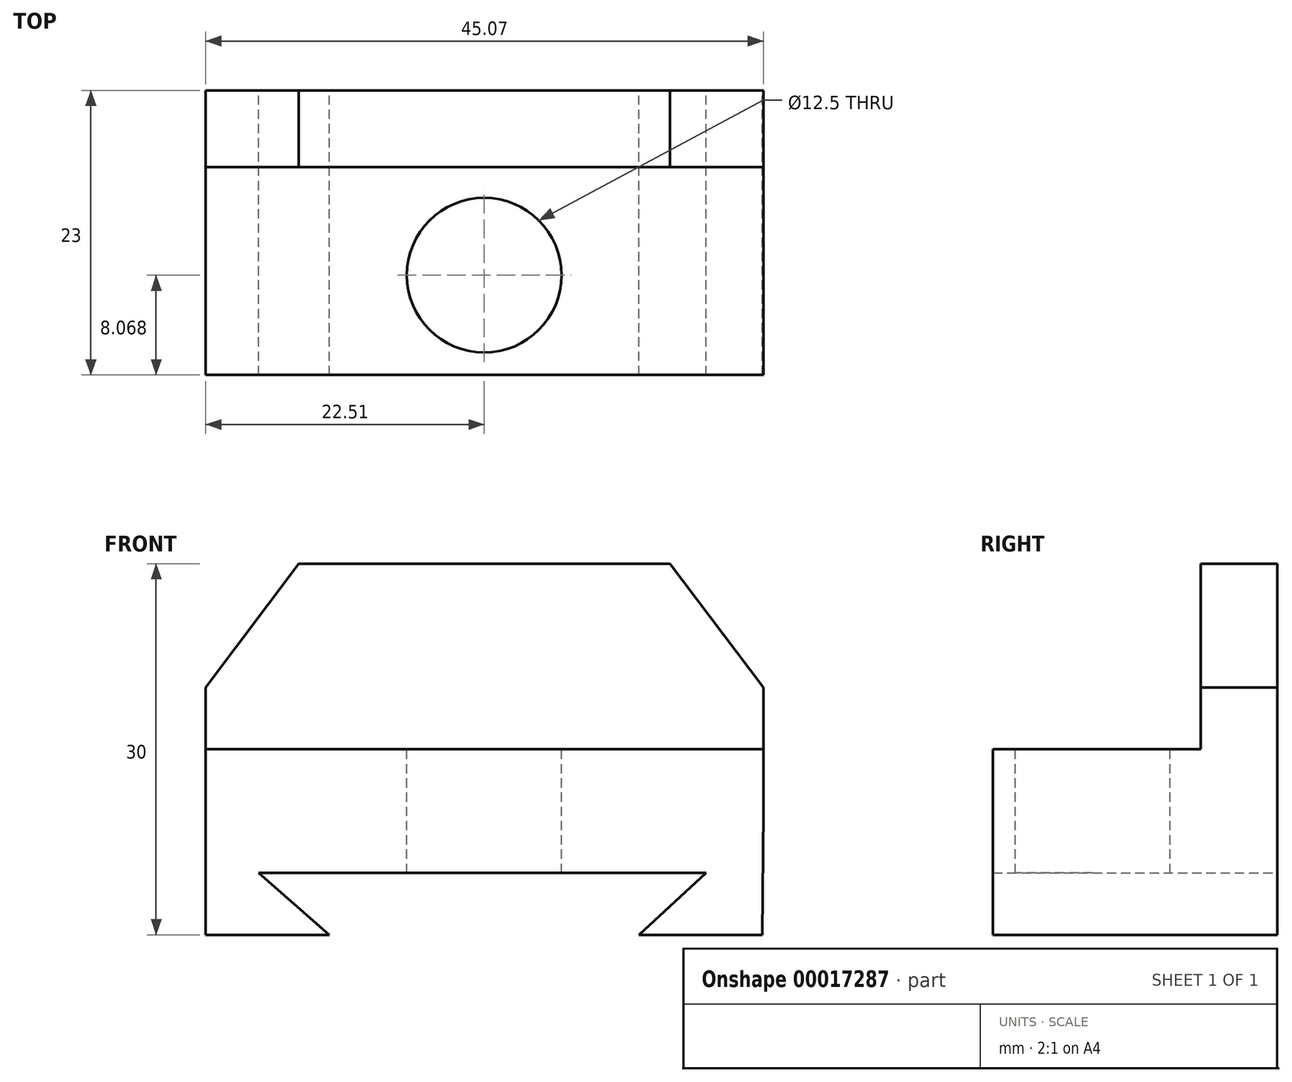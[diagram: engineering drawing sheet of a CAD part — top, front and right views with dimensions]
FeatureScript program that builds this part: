
annotation { "Feature Type Name" : "Feature", "Feature Type Description" : "" }
export const myFeature = defineFeature(function(context is Context, id is Id, definition is map)
    precondition{}
    {
        {
            var Q0;
            Q0=qCreatedBy(makeId("Front.planeOp"),FACE);
            var sketch = newSketch(context, id + "F0", { "sketchPlane" : qUnion([Q0])});
            skLineSegment(sketch, "E0", {"start": v(22.49, -30) * mm, "end": v(22.56, -20) * mm});
            skLineSegment(sketch, "E1", {"start": v(22.56, -20) * mm, "end": v(22.56, -15) * mm});
            skLineSegment(sketch, "E2", {"start": v(-22.58, -30.8) * mm, "end": v(-22.51, -30) * mm});
            skLineSegment(sketch, "E3", {"start": v(-22.51, -30) * mm, "end": v(-22.51, -20) * mm});
            skLineSegment(sketch, "E4", {"start": v(-22.51, -20) * mm, "end": v(-22.51, -15) * mm});
            skLineSegment(sketch, "E5", {"start": v(-22.51, -15) * mm, "end": v(22.56, -15) * mm});
            skLineSegment(sketch, "E6", {"start": v(-22.51, -15) * mm, "end": v(-22.51, -10) * mm});
            skLineSegment(sketch, "E7", {"start": v(22.56, -15) * mm, "end": v(22.56, -10) * mm});
            skLineSegment(sketch, "E8", {"start": v(0, 0) * mm, "end": v(15, 0) * mm});
            skLineSegment(sketch, "E9", {"start": v(0, 0) * mm, "end": v(-15, 0) * mm});
            skLineSegment(sketch, "E10", {"start": v(-22.51, -10) * mm, "end": v(-15, 0) * mm});
            skLineSegment(sketch, "E11", {"start": v(15, 0) * mm, "end": v(22.56, -10) * mm});
            skLineSegment(sketch, "E12", {"start": v(-22.51, -30) * mm, "end": v(-12.51, -30) * mm});
            skLineSegment(sketch, "E13", {"start": v(22.49, -30) * mm, "end": v(12.49, -30) * mm});
            skLineSegment(sketch, "E14", {"start": v(-12.51, -30) * mm, "end": v(-18.22, -25) * mm});
            skLineSegment(sketch, "E15", {"start": v(12.49, -30) * mm, "end": v(17.92, -25) * mm});
            skLineSegment(sketch, "E16", {"start": v(17.92, -25) * mm, "end": v(-18.22, -25) * mm});
            skSolve(sketch);
        }
        {
            var Q0;
            Q0=makeQuery(id+"F0.imprint","IMPRINT",FACE,{"disambiguationData":[TD([[makeQuery(id+"F0.imprint","IMPRINT",EDGE,{"derivedFrom":sQuery(id+"F0.wireOp",EDGE,"E0")}),1.0]])]});
            extrude(context, id + "F1", {"entities" : qUnion([Q0]), "depth" : 23 * mm});
        }
        {
            var Q0;
            Q0=makeQuery(id+"F0.imprint","IMPRINT",FACE,{"disambiguationData":[TD([[makeQuery(id+"F0.imprint","IMPRINT",EDGE,{"derivedFrom":sQuery(id+"F0.wireOp",EDGE,"E5")}),1.0]])]});
            var sketch = newSketch(context, id + "F2", { "sketchPlane" : qUnion([Q0])});
            skSolve(sketch);
        }
        {
            var Q0;
            Q0 = qSketchRegion(id + "F2", true);
            var Q1;
            Q1=makeQuery(id+"F0.imprint","IMPRINT",FACE,{"disambiguationData":[TD([[makeQuery(id+"F0.imprint","IMPRINT",EDGE,{"derivedFrom":sQuery(id+"F0.wireOp",EDGE,"E5")}),1.0]])]});
            extrude(context, id + "F3", {"entities" : qUnion([Q0, Q1]), "operationType" : NewBodyOperationType.ADD, "depth" : 6.2 * mm});
        }
        {
            var Q0;
            Q0=makeQuery(id+"F1.opExtrude","SWEPT_FACE",FACE,{"disambiguationData":[OSD([sQuery(id+"F0.wireOp",EDGE,"E5")])]});
            var sketch = newSketch(context, id + "F4", { "sketchPlane" : qUnion([Q0])});
            skCircle(sketch, "E17", {"center": v(0, -14.93) * mm, "radius": 4.8 * mm});
            skSolve(sketch);
        }
        {
            var Q0;
            Q0=sQuery(id+"F4.wireOp",VERTEX,"E17.center");
            var Q1;
            Q1=makeQuery(id+"F1.opExtrude","SWEPT_BODY",BODY,{"disambiguationData":[OSD([sQuery(id+"F0.wireOp",EDGE,"E0"),sQuery(id+"F0.wireOp",EDGE,"E1"),sQuery(id+"F0.wireOp",EDGE,"E3"),sQuery(id+"F0.wireOp",EDGE,"E4"),sQuery(id+"F0.wireOp",EDGE,"E5"),sQuery(id+"F0.wireOp",EDGE,"E12"),sQuery(id+"F0.wireOp",EDGE,"E13"),sQuery(id+"F0.wireOp",EDGE,"E14"),sQuery(id+"F0.wireOp",EDGE,"E15"),sQuery(id+"F0.wireOp",EDGE,"E16")])]});
            hole(context, id + "F5", {"style" : HoleStyle.SIMPLE, "holeDiameter" : 12.5 * mm, "endStyle" : HoleEndStyle.THROUGH, "locations" : qUnion([Q0]), "scope" : qUnion([Q1])});
        }
    });
